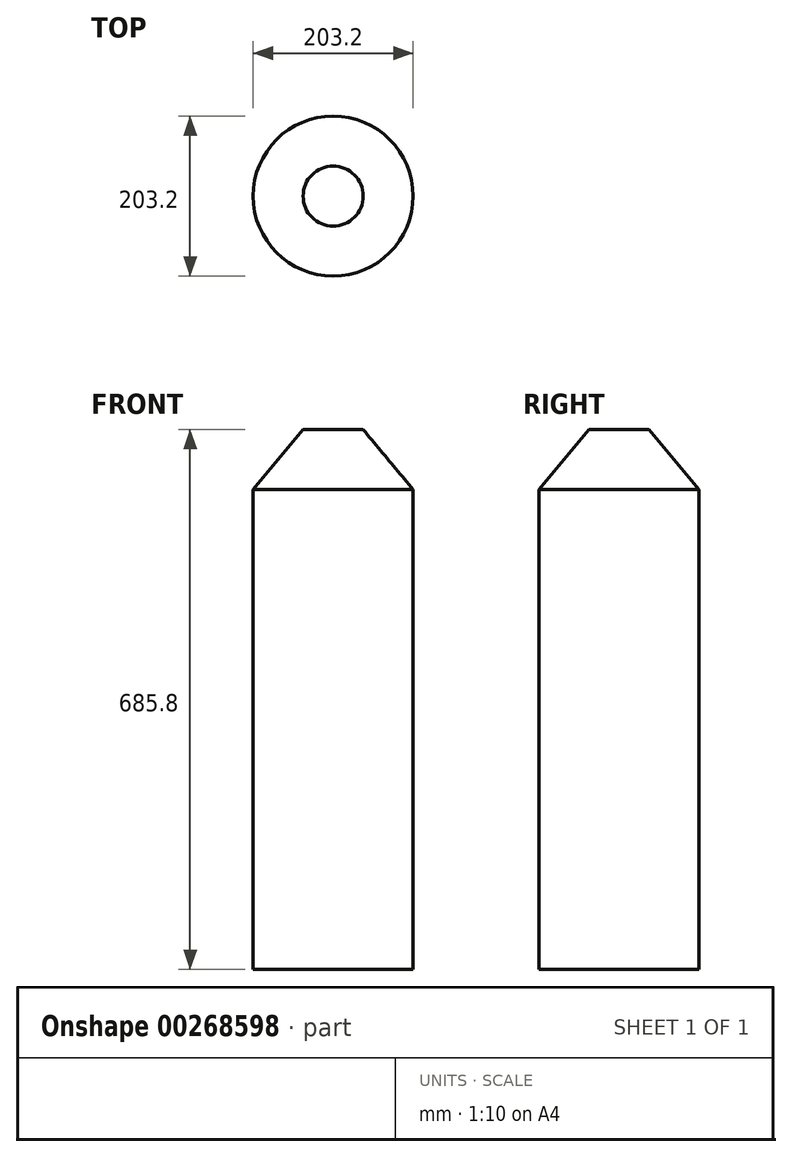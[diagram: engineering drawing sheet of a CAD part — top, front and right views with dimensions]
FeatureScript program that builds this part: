
annotation { "Feature Type Name" : "Feature", "Feature Type Description" : "" }
export const myFeature = defineFeature(function(context is Context, id is Id, definition is map)
    precondition{}
    {
        {
            var Q0;
            Q0=qCreatedBy(makeId("Top.planeOp"),FACE);
            var sketch = newSketch(context, id + "F0", { "sketchPlane" : qUnion([Q0])});
            skCircle(sketch, "E0", {"center": v(0, 0) * mm, "radius": 101.6 * mm});
            skSolve(sketch);
        }
        {
            var Q0;
            Q0=makeQuery(id+"F0.imprint","IMPRINT",FACE,{"disambiguationData":[TD([[makeQuery(id+"F0.imprint","IMPRINT",EDGE,{"derivedFrom":sQuery(id+"F0.wireOp",EDGE,"E0")}),1.0]])]});
            extrude(context, id + "F1", {"entities" : qUnion([Q0]), "depth" : 609.6 * mm, "offsetDistance" : 25.4 * mm});
        }
        {
            var Q0;
            Q0=qCreatedBy(makeId("Top.planeOp"),FACE);
            cPlane(context, id + "F2", {"entities" : qUnion([Q0]), "cplaneType" : CPlaneType.OFFSET, "offset" : 685.8 * mm, "width" : 152.4 * mm, "height" : 152.4 * mm});
        }
        {
            var Q0;
            Q0=qCreatedBy(id+"F2.planeOp",FACE);
            var sketch = newSketch(context, id + "F3", { "sketchPlane" : qUnion([Q0])});
            skCircle(sketch, "E1", {"center": v(0, 0) * mm, "radius": 38.1 * mm});
            skSolve(sketch);
        }
        {
            var Q0;
            Q0=makeQuery(id+"F1.opExtrude","CAP_FACE",FACE,{"disambiguationData":[OSD([sQuery(id+"F0.wireOp",EDGE,"E0")])],"isStart":false});
            var sketch = newSketch(context, id + "F4", { "sketchPlane" : qUnion([Q0])});
            skCircle(sketch, "E2", {"center": v(0, 0) * mm, "radius": 101.6 * mm});
            skSolve(sketch);
        }
        {
            var Q0;
            Q0=makeQuery(id+"F4.imprint","IMPRINT",FACE,{"disambiguationData":[TD([[makeQuery(id+"F4.imprint","IMPRINT",EDGE,{"derivedFrom":sQuery(id+"F4.wireOp",EDGE,"E2")}),1.0]])]});
            var Q1;
            Q1=makeQuery(id+"F3.imprint","IMPRINT",FACE,{"disambiguationData":[TD([[makeQuery(id+"F3.imprint","IMPRINT",EDGE,{"derivedFrom":sQuery(id+"F3.wireOp",EDGE,"E1")}),1.0]])]});
            loft(context, id + "F5", {"operationType" : NewBodyOperationType.ADD, "sheetProfilesArray" : [{ "sheetProfileEntities" : qUnion([Q0]) }, { "sheetProfileEntities" : qUnion([Q1]) }]});
        }
    });
